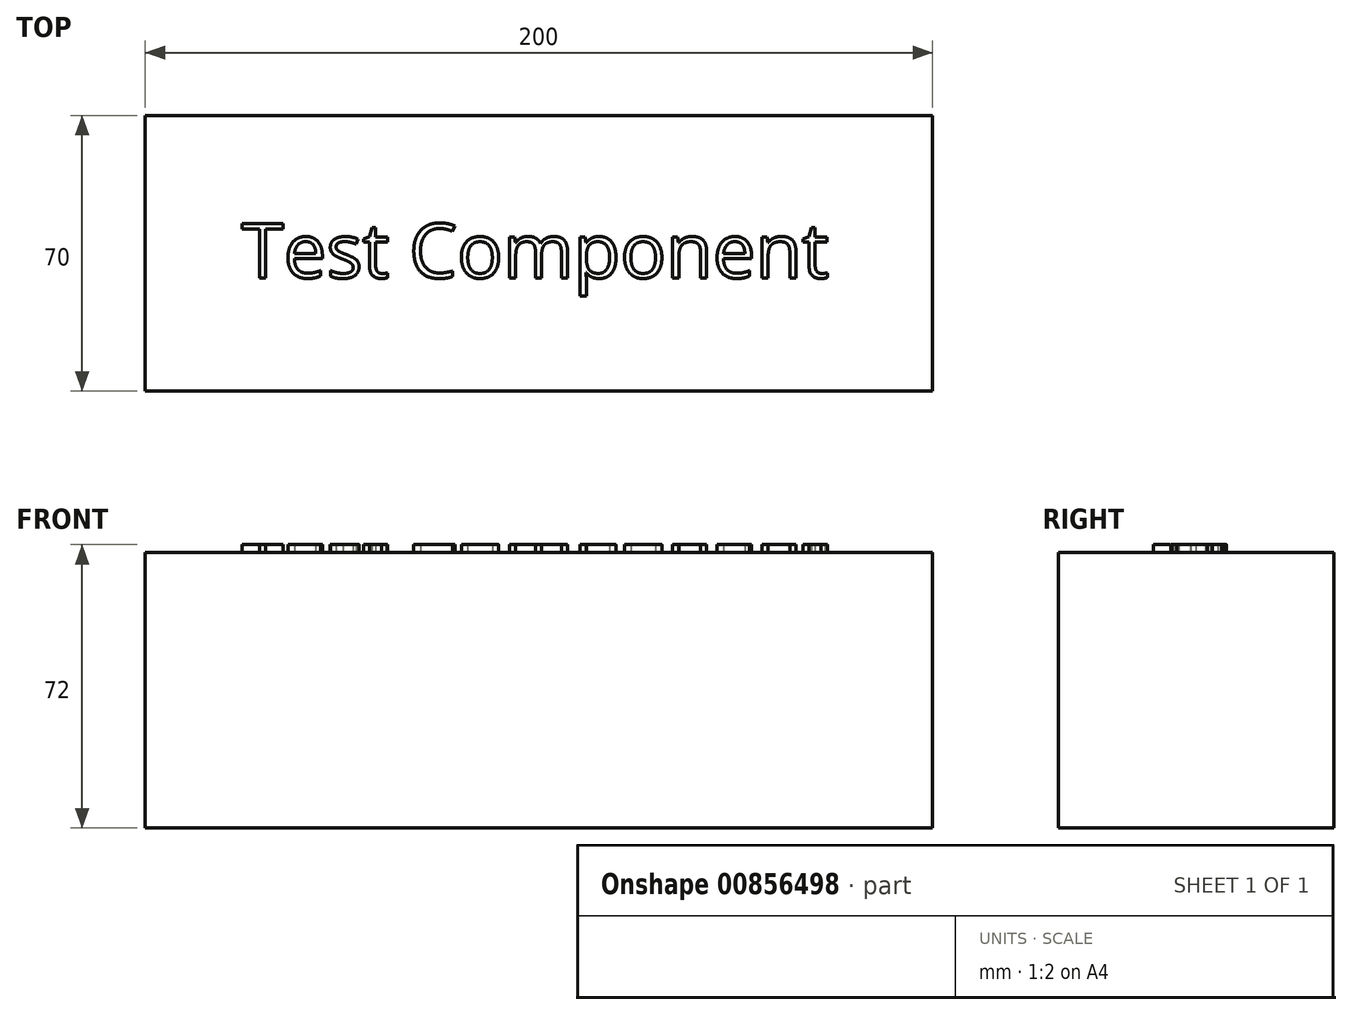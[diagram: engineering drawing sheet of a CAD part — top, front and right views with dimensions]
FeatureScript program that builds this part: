
annotation { "Feature Type Name" : "Feature", "Feature Type Description" : "" }
export const myFeature = defineFeature(function(context is Context, id is Id, definition is map)
    precondition{}
    {
        {
            var Q0;
            Q0=qCreatedBy(makeId("Top.planeOp"),FACE);
            var sketch = newSketch(context, id + "F0", { "sketchPlane" : qUnion([Q0])});
            skLineSegment(sketch, "E0.bottom", {"start": v(100, -35) * mm, "end": v(-100, -35) * mm});
            skLineSegment(sketch, "E0.top", {"start": v(100, 35) * mm, "end": v(-100, 35) * mm});
            skLineSegment(sketch, "E0.left", {"start": v(100, -35) * mm, "end": v(100, 35) * mm});
            skLineSegment(sketch, "E0.right", {"start": v(-100, -35) * mm, "end": v(-100, 35) * mm});
            skPoint(sketch, "E0.middle", {"position": v(0, 0) * mm});
            skSolve(sketch);
        }
        {
            var Q0;
            Q0 = qSketchRegion(id + "F0", true);
            extrude(context, id + "F1", {"entities" : qUnion([Q0]), "depth" : 70 * mm, "offsetDistance" : 25 * mm});
        }
        {
            var Q0;
            Q0=makeQuery(id+"F1.opExtrude","CAP_FACE",FACE,{"disambiguationData":[OSD([sQuery(id+"F0.wireOp",EDGE,"E0.bottom"),sQuery(id+"F0.wireOp",EDGE,"E0.top"),sQuery(id+"F0.wireOp",EDGE,"E0.left"),sQuery(id+"F0.wireOp",EDGE,"E0.right")])],"isStart":false});
            cPlane(context, id + "F2", {"entities" : qUnion([Q0]), "cplaneType" : CPlaneType.OFFSET, "offset" : 0 * mm, "width" : 150 * mm, "height" : 150 * mm});
        }
        {
            var Q0;
            Q0=qCreatedBy(id+"F2.planeOp",FACE);
            var sketch = newSketch(context, id + "F3", { "sketchPlane" : qUnion([Q0])});
            skText(sketch, "E1", { "text": "Test Component", "fontName": "OpenSans-Regular.ttf"});
            const initialGuessF3  = {"E1": [-0.0755, -0.00624, 1, 0, 0.0139]};
            skSetInitialGuess(sketch, initialGuessF3);
            skSolve(sketch);
        }
        {
            var Q0;
            Q0 = qSketchRegion(id + "F3", true);
            extrude(context, id + "F4", {"entities" : qUnion([Q0]), "operationType" : NewBodyOperationType.ADD, "depth" : 2 * mm, "offsetDistance" : 25 * mm});
        }
    });
